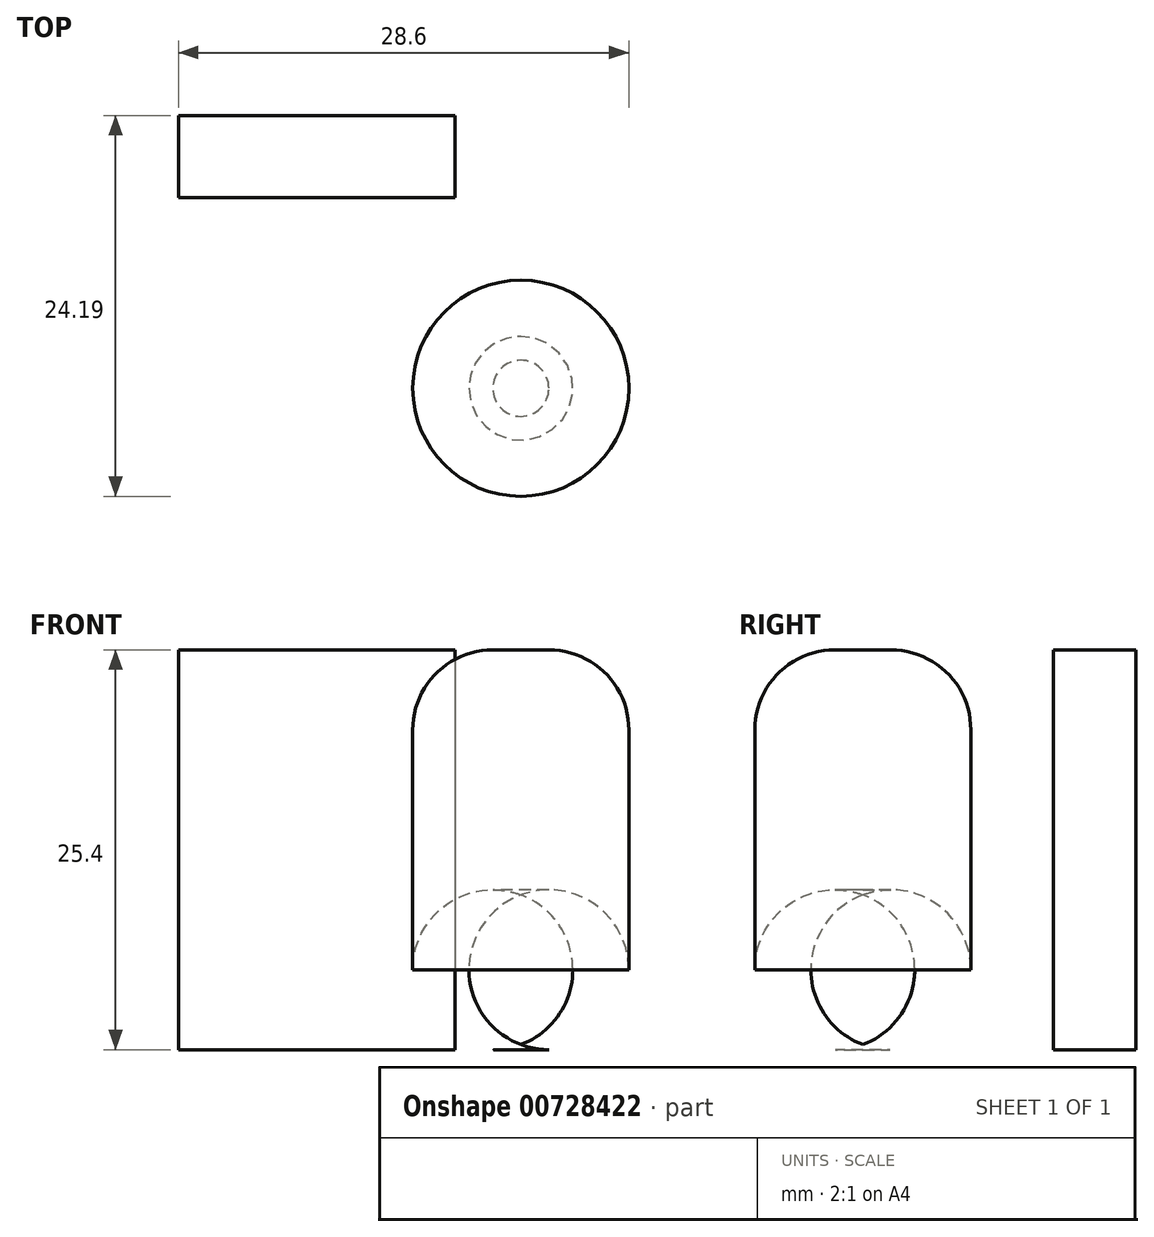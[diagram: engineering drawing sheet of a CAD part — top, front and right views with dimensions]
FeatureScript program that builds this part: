
annotation { "Feature Type Name" : "Feature", "Feature Type Description" : "" }
export const myFeature = defineFeature(function(context is Context, id is Id, definition is map)
    precondition{}
    {
        {
            var Q0;
            Q0=qCreatedBy(makeId("Top.planeOp"),FACE);
            var sketch = newSketch(context, id + "F0", { "sketchPlane" : qUnion([Q0])});
            skCircle(sketch, "E0", {"center": v(0, 0) * mm, "radius": 6.86 * mm});
            skSolve(sketch);
        }
        {
            var Q0;
            Q0=qCreatedBy(makeId("Top.planeOp"),FACE);
            var sketch = newSketch(context, id + "F1", { "sketchPlane" : qUnion([Q0])});
            skLineSegment(sketch, "E1.bottom", {"start": v(-21.74, 17.33) * mm, "end": v(-4.18, 17.33) * mm});
            skLineSegment(sketch, "E1.top", {"start": v(-21.74, 12.1) * mm, "end": v(-4.18, 12.1) * mm});
            skLineSegment(sketch, "E1.left", {"start": v(-21.74, 17.33) * mm, "end": v(-21.74, 12.1) * mm});
            skLineSegment(sketch, "E1.right", {"start": v(-4.18, 17.33) * mm, "end": v(-4.18, 12.1) * mm});
            skSolve(sketch);
        }
        {
            var Q0;
            Q0 = qSketchRegion(id + "F1", true);
            extrude(context, id + "F2", {"entities" : qUnion([Q0]), "depth" : 25.4 * mm, "offsetDistance" : 25.4 * mm});
        }
        {
            var Q0;
            Q0=makeQuery(id+"F0.imprint","IMPRINT",FACE,{"disambiguationData":[TD([[makeQuery(id+"F0.imprint","IMPRINT",EDGE,{"derivedFrom":sQuery(id+"F0.wireOp",EDGE,"E0")}),1.0]])]});
            extrude(context, id + "F3", {"entities" : qUnion([Q0]), "depth" : 25.4 * mm, "offsetDistance" : 25.4 * mm});
        }
        {
            var Q0;
            Q0=qCreatedBy(makeId("Top.planeOp"),FACE);
            var sketch = newSketch(context, id + "F4", { "sketchPlane" : qUnion([Q0])});
            skCircle(sketch, "E2", {"center": v(0, 0) * mm, "radius": 3.93 * mm});
            skSolve(sketch);
        }
        {
            var Q0;
            Q0=sQuery(id+"F4.wireOp",EDGE,"E2");
            extrude(context, id + "F5", {"bodyType" : ToolBodyType.SURFACE, "surfaceEntities" : qUnion([Q0]), "oppositeDirection" : true, "depth" : 21.3 * mm, "offsetDistance" : 25.4 * mm});
        }
        {
            var Q0;
            Q0=makeQuery(id+"F3.opExtrude","SWEPT_FACE",FACE,{"disambiguationData":[OSD([sQuery(id+"F0.wireOp",EDGE,"E0")])]});
            fillet(context, id + "F6", {"entities" : qUnion([Q0]), "radius" : 5.08 * mm, "tangentPropagation" : true, "allowEdgeOverflow" : false});
        }
    });
